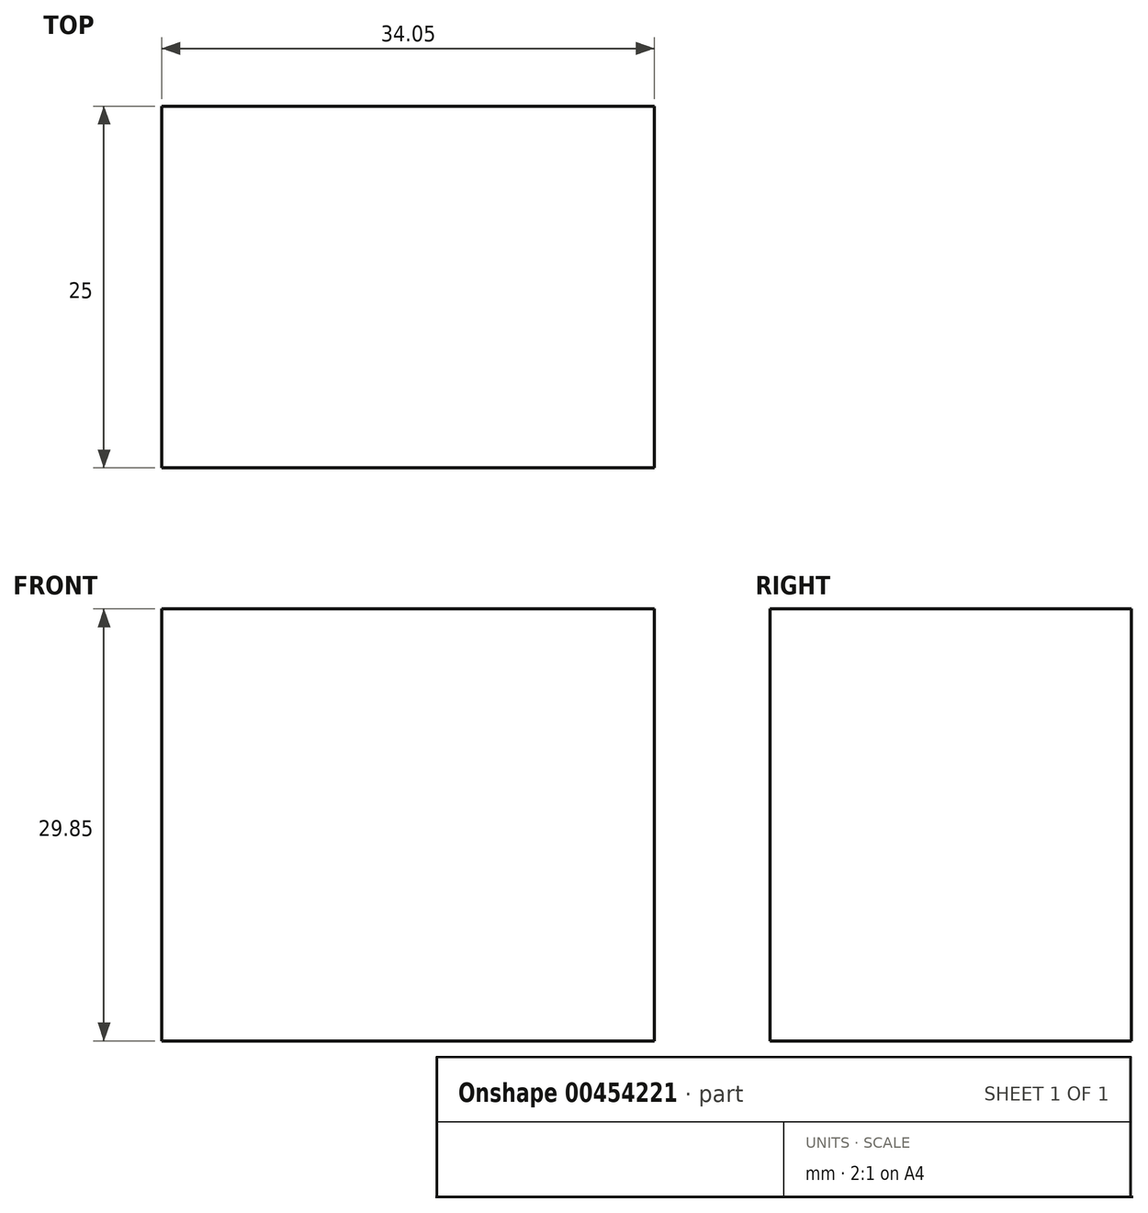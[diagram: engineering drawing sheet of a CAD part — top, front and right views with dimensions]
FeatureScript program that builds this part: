
annotation { "Feature Type Name" : "Feature", "Feature Type Description" : "" }
export const myFeature = defineFeature(function(context is Context, id is Id, definition is map)
    precondition{}
    {
        {
            var Q0;
            Q0=qCreatedBy(makeId("Front.planeOp"),FACE);
            var sketch = newSketch(context, id + "F0", { "sketchPlane" : qUnion([Q0])});
            skLineSegment(sketch, "E0.bottom", {"start": v(-90.46, 21.62) * mm, "end": v(-56.41, 21.62) * mm});
            skLineSegment(sketch, "E0.top", {"start": v(-90.46, 51.47) * mm, "end": v(-56.41, 51.47) * mm});
            skLineSegment(sketch, "E0.left", {"start": v(-90.46, 21.62) * mm, "end": v(-90.46, 51.47) * mm});
            skLineSegment(sketch, "E0.right", {"start": v(-56.41, 21.62) * mm, "end": v(-56.41, 51.47) * mm});
            skPoint(sketch, "E0.middle", {"position": v(-73.43, 36.55) * mm});
            skSolve(sketch);
        }
        {
            var Q0;
            Q0=makeQuery(id+"F0.imprint","IMPRINT",FACE,{"disambiguationData":[TD([[makeQuery(id+"F0.imprint","IMPRINT",EDGE,{"derivedFrom":sQuery(id+"F0.wireOp",EDGE,"E0.bottom")}),1.0]])]});
            extrude(context, id + "F1", {"entities" : qUnion([Q0]), "depth" : 25 * mm});
        }
    });
